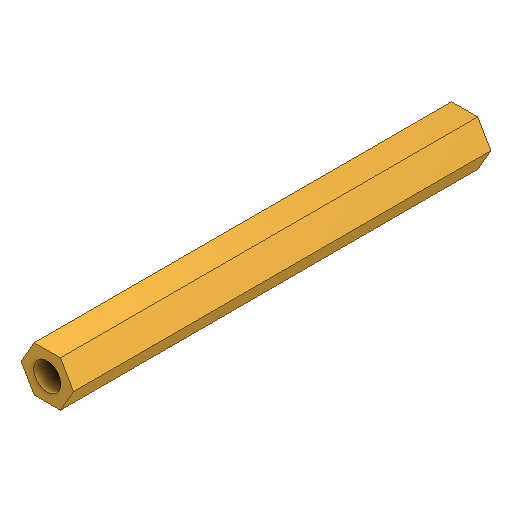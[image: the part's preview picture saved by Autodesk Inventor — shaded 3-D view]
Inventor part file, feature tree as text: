
AUTODESK INVENTOR PART (.ipt)
format: ipt  version: 2025.2 (Build 292293000, 293)  size: 108,032 bytes
history: native  units: mm
features: extrude x1, sketch x1
ambient origin geometry x8: Origin, YZ Plane, XZ Plane, XY Plane, X Axis, Y Axis, Z Axis, Center Point
bodies: Solid1 (feature_tree)
feature tree (2):
  extrude  "Extrusion1"  Depth=46.0mm
  sketch  "Sketch1"  dims[d0=5.0mm d1=3.0mm d2=46.0mm d3=0.0mm]
